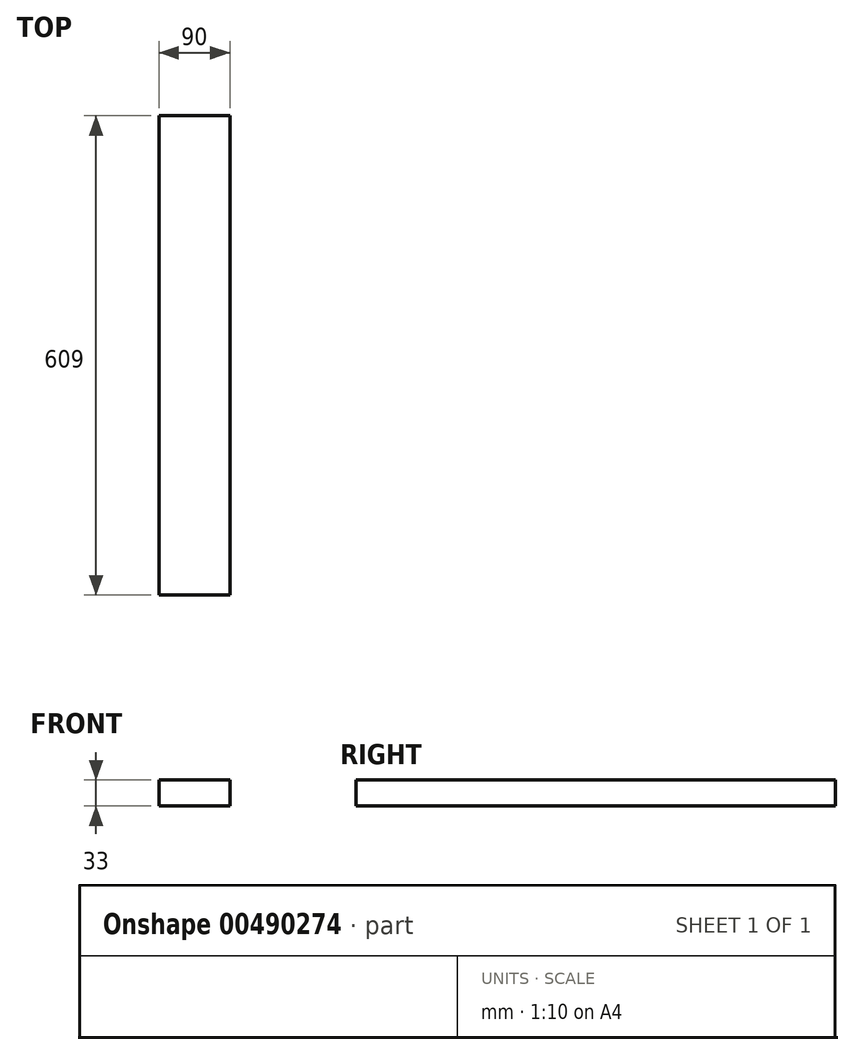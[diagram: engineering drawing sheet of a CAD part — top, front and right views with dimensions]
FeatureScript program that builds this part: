
annotation { "Feature Type Name" : "Feature", "Feature Type Description" : "" }
export const myFeature = defineFeature(function(context is Context, id is Id, definition is map)
    precondition{}
    {
        {
            var Q0;
            Q0=qCreatedBy(makeId("Front.planeOp"),FACE);
            var sketch = newSketch(context, id + "F0", { "sketchPlane" : qUnion([Q0])});
            skLineSegment(sketch, "E0.bottom", {"start": v(0, 0) * mm, "end": v(-90, 0) * mm});
            skLineSegment(sketch, "E0.top", {"start": v(0, 33) * mm, "end": v(-90, 33) * mm});
            skLineSegment(sketch, "E0.left", {"start": v(0, 0) * mm, "end": v(0, 33) * mm});
            skLineSegment(sketch, "E0.right", {"start": v(-90, 0) * mm, "end": v(-90, 33) * mm});
            skSolve(sketch);
        }
        {
            var Q0;
            Q0=makeQuery(id+"F0.imprint","IMPRINT",FACE,{"disambiguationData":[TD([[makeQuery(id+"F0.imprint","IMPRINT",EDGE,{"derivedFrom":sQuery(id+"F0.wireOp",EDGE,"E0.bottom")}),-1.0]])]});
            extrude(context, id + "F1", {"entities" : qUnion([Q0]), "depth" : 609 * mm});
        }
    });
